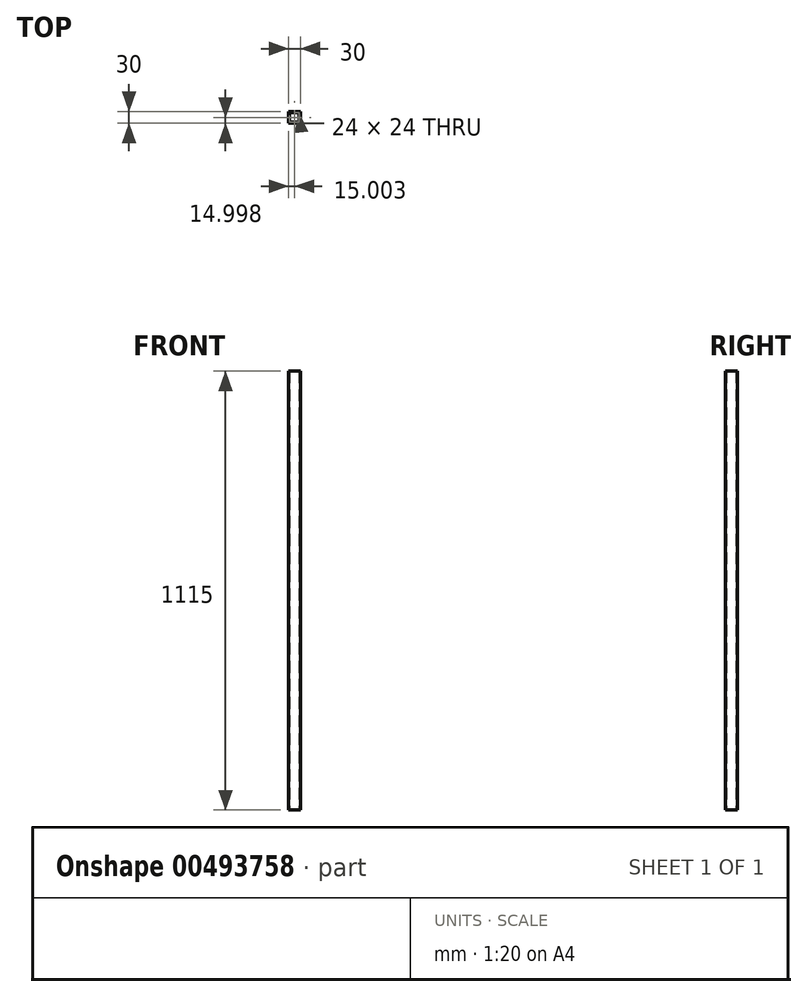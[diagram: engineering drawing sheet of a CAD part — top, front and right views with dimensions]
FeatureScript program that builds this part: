
annotation { "Feature Type Name" : "Feature", "Feature Type Description" : "" }
export const myFeature = defineFeature(function(context is Context, id is Id, definition is map)
    precondition{}
    {
        {
            var Q0;
            Q0=qCreatedBy(makeId("Top.planeOp"),FACE);
            var sketch = newSketch(context, id + "F0", { "sketchPlane" : qUnion([Q0])});
            skLineSegment(sketch, "E0.bottom", {"start": v(-15.76, 12.18) * mm, "end": v(8.24, 12.18) * mm});
            skLineSegment(sketch, "E0.top", {"start": v(-15.76, -11.82) * mm, "end": v(8.24, -11.82) * mm});
            skLineSegment(sketch, "E0.left", {"start": v(-15.76, 12.18) * mm, "end": v(-15.76, -11.82) * mm});
            skLineSegment(sketch, "E0.right", {"start": v(8.24, 12.18) * mm, "end": v(8.24, -11.82) * mm});
            skLineSegment(sketch, "E1.bottom", {"start": v(-18.76, 15.18) * mm, "end": v(11.24, 15.18) * mm});
            skLineSegment(sketch, "E1.top", {"start": v(-18.76, -14.82) * mm, "end": v(11.24, -14.82) * mm});
            skLineSegment(sketch, "E1.left", {"start": v(-18.76, 15.18) * mm, "end": v(-18.76, -14.82) * mm});
            skLineSegment(sketch, "E1.right", {"start": v(11.24, 15.18) * mm, "end": v(11.24, -14.82) * mm});
            skSolve(sketch);
        }
        {
            var Q0;
            Q0=qSketchRegion(id+"F0",true);
            extrude(context, id + "F1", {"entities" : qUnion([Q0]), "offsetDistance" : 25 * mm, "depth" : 1115 * mm});
        }
    });
